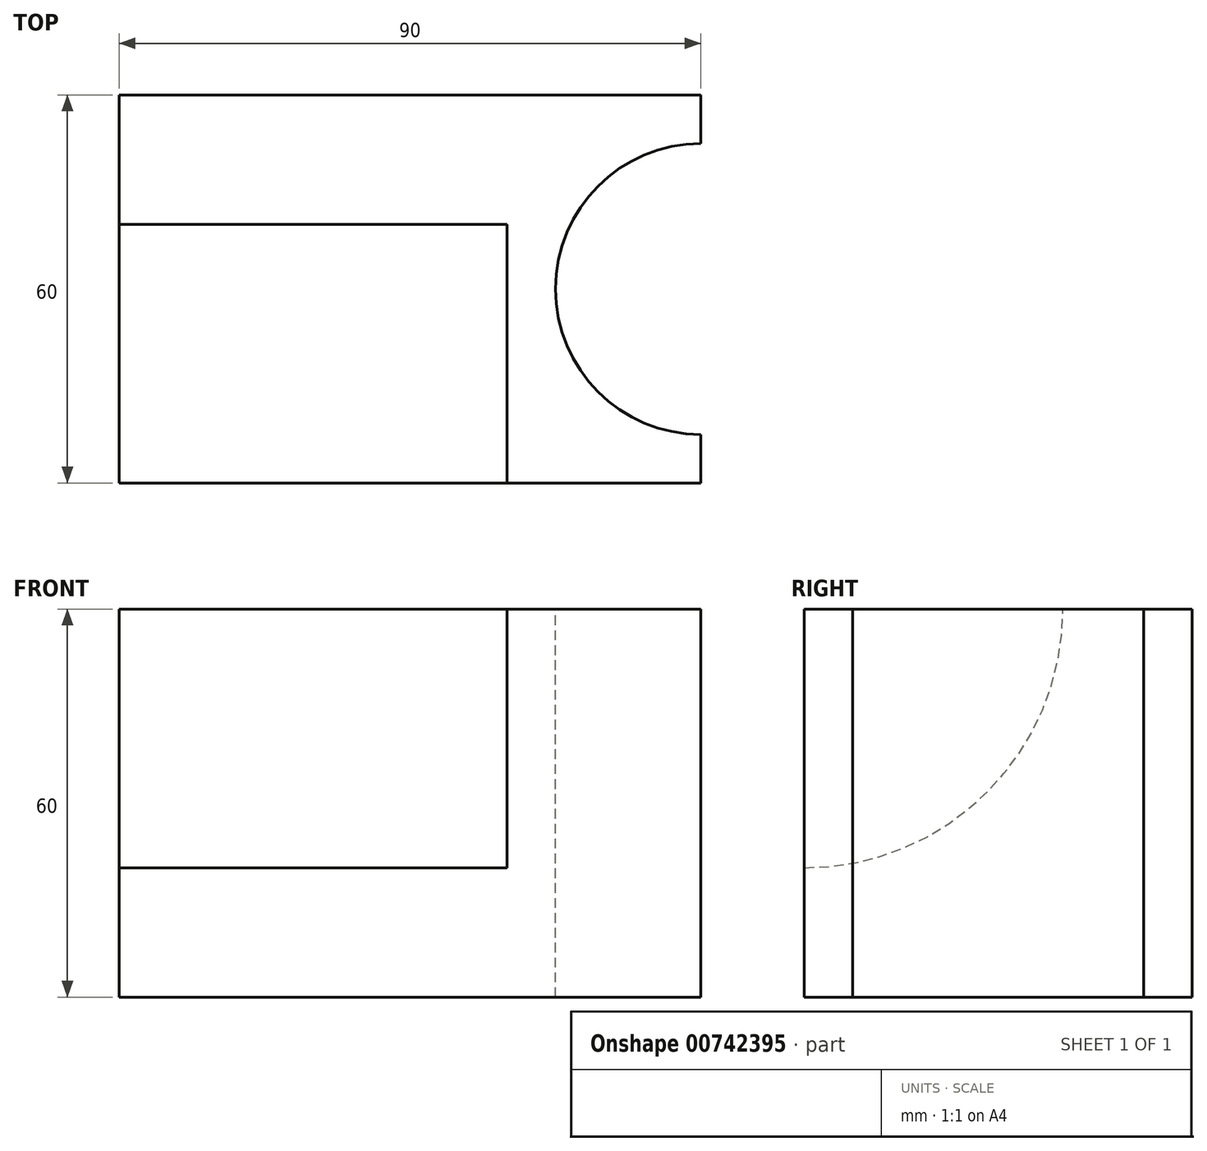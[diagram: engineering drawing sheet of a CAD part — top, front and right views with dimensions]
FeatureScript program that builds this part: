
annotation { "Feature Type Name" : "Feature", "Feature Type Description" : "" }
export const myFeature = defineFeature(function(context is Context, id is Id, definition is map)
    precondition{}
    {
        {
            var Q0;
            Q0=qCreatedBy(makeId("Front.planeOp"),FACE);
            var sketch = newSketch(context, id + "F0", { "sketchPlane" : qUnion([Q0])});
            skLineSegment(sketch, "E0.bottom", {"start": v(0, 0) * mm, "end": v(90, 0) * mm});
            skLineSegment(sketch, "E0.top", {"start": v(0, 60) * mm, "end": v(90, 60) * mm});
            skLineSegment(sketch, "E0.left", {"start": v(0, 0) * mm, "end": v(0, 60) * mm});
            skLineSegment(sketch, "E0.right", {"start": v(90, 0) * mm, "end": v(90, 60) * mm});
            skSolve(sketch);
        }
        {
            var Q0;
            Q0 = qSketchRegion(id + "F0", true);
            extrude(context, id + "F1", {"entities" : qUnion([Q0]), "depth" : 60 * mm, "offsetDistance" : 25 * mm});
        }
        {
            var Q0;
            Q0=makeQuery(id+"F1.opExtrude","SWEPT_FACE",FACE,{"disambiguationData":[OSD([sQuery(id+"F0.wireOp",EDGE,"E0.left")])]});
            var sketch = newSketch(context, id + "F2", { "sketchPlane" : qUnion([Q0])});
            skArc(sketch, "E1", {"start": v(20, 60) * mm, "mid": v(31.72, 31.72) * mm, "end": v(60, 20) * mm});
            skSolve(sketch);
        }
        {
            var Q0;
            {var subQ0=sQuery(id+"F2.wireOp",EDGE,"E1");Q0=makeQuery(id+"F2.imprint","IMPRINT",FACE,{"disambiguationData":[TD([[makeQuery(id+"F2.imprint","IMPRINT",EDGE,{"derivedFrom":subQ0}),1.0]])]});}
            extrude(context, id + "F3", {"entities" : qUnion([Q0]), "operationType" : NewBodyOperationType.REMOVE, "oppositeDirection" : true, "depth" : 60 * mm, "offsetDistance" : 25 * mm});
        }
        {
            var Q0;
            Q0=makeQuery(id+"F1.opExtrude","SWEPT_FACE",FACE,{"disambiguationData":[OSD([sQuery(id+"F0.wireOp",EDGE,"E0.top")])]});
            var sketch = newSketch(context, id + "F4", { "sketchPlane" : qUnion([Q0])});
            skArc(sketch, "E2", {"start": v(90, -7.5) * mm, "mid": v(67.5, -30) * mm, "end": v(90, -52.5) * mm});
            skSolve(sketch);
        }
        {
            var Q0;
            {var subQ0=sQuery(id+"F4.wireOp",EDGE,"E2");Q0=makeQuery(id+"F4.imprint","IMPRINT",FACE,{"disambiguationData":[TD([[makeQuery(id+"F4.imprint","IMPRINT",EDGE,{"derivedFrom":subQ0}),1.0]])]});}
            extrude(context, id + "F5", {"entities" : qUnion([Q0]), "operationType" : NewBodyOperationType.REMOVE, "endBound" : BoundingType.THROUGH_ALL, "oppositeDirection" : true, "depth" : 25 * mm, "offsetDistance" : 25 * mm});
        }
    });
